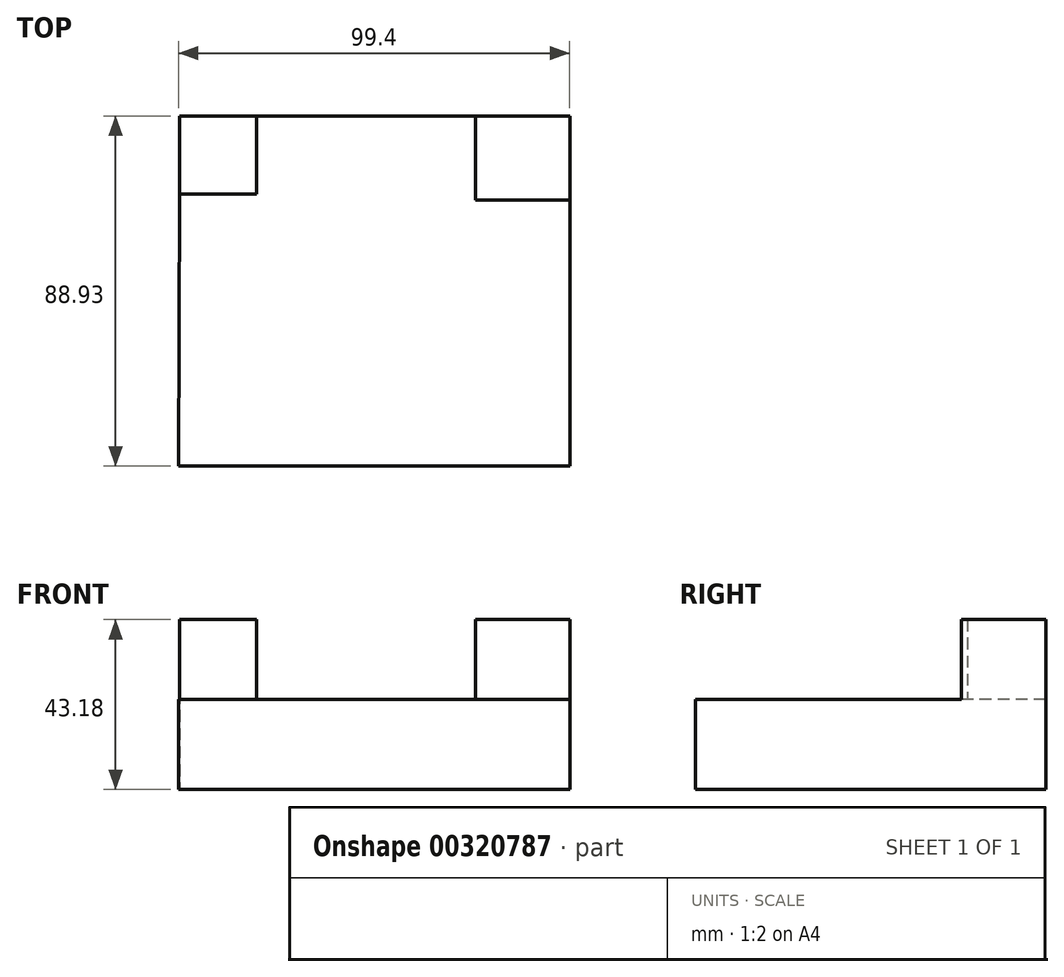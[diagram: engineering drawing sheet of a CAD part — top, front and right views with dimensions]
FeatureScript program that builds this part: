
annotation { "Feature Type Name" : "Feature", "Feature Type Description" : "" }
export const myFeature = defineFeature(function(context is Context, id is Id, definition is map)
    precondition{}
    {
        {
            var Q0;
            Q0=qCreatedBy(makeId("Top.planeOp"),FACE);
            var sketch = newSketch(context, id + "F0", { "sketchPlane" : qUnion([Q0])});
            skLineSegment(sketch, "E0", {"start": v(-45.8, -41.68) * mm, "end": v(53.6, -41.68) * mm});
            skLineSegment(sketch, "E1", {"start": v(53.6, -41.68) * mm, "end": v(53.6, 47.25) * mm});
            skLineSegment(sketch, "E2", {"start": v(53.6, 47.25) * mm, "end": v(-45.5, 47.25) * mm});
            skLineSegment(sketch, "E3", {"start": v(-45.8, -41.68) * mm, "end": v(-45.5, 47.25) * mm});
            skSolve(sketch);
        }
        {
            var Q0;
            Q0=makeQuery(id+"F0.imprint","IMPRINT",FACE,{"disambiguationData":[TD([[makeQuery(id+"F0.imprint","IMPRINT",EDGE,{"derivedFrom":sQuery(id+"F0.wireOp",EDGE,"E0")}),1.0]])]});
            extrude(context, id + "F1", {"entities" : qUnion([Q0]), "depth" : 22.86 * mm});
        }
        {
            var Q0;
            Q0=makeQuery(id+"F1.opExtrude","CAP_FACE",FACE,{"disambiguationData":[OSD([sQuery(id+"F0.wireOp",EDGE,"E0"),sQuery(id+"F0.wireOp",EDGE,"E1"),sQuery(id+"F0.wireOp",EDGE,"E2"),sQuery(id+"F0.wireOp",EDGE,"E3")])],"isStart":false});
            var sketch = newSketch(context, id + "F2", { "sketchPlane" : qUnion([Q0])});
            skLineSegment(sketch, "E4", {"start": v(29.71, 47.25) * mm, "end": v(29.71, 25.84) * mm});
            skLineSegment(sketch, "E5", {"start": v(29.71, 25.84) * mm, "end": v(53.6, 25.84) * mm});
            skSolve(sketch);
        }
        {
            var Q0;
            {var subQ0=sQuery(id+"F2.wireOp",EDGE,"E4");Q0=makeQuery(id+"F2.imprint","IMPRINT",FACE,{"disambiguationData":[TD([[makeQuery(id+"F2.imprint","IMPRINT",EDGE,{"derivedFrom":subQ0}),1.0]])]});}
            extrude(context, id + "F3", {"entities" : qUnion([Q0]), "operationType" : NewBodyOperationType.ADD, "depth" : 20.32 * mm});
        }
        {
            var Q0;
            Q0=makeQuery(id+"F1.opExtrude","CAP_FACE",FACE,{"disambiguationData":[OSD([sQuery(id+"F0.wireOp",EDGE,"E0"),sQuery(id+"F0.wireOp",EDGE,"E1"),sQuery(id+"F0.wireOp",EDGE,"E2"),sQuery(id+"F0.wireOp",EDGE,"E3")])],"isStart":false});
            var sketch = newSketch(context, id + "F4", { "sketchPlane" : qUnion([Q0])});
            skLineSegment(sketch, "E6", {"start": v(-26, 47.25) * mm, "end": v(-26, 27.4) * mm});
            skLineSegment(sketch, "E7", {"start": v(-26, 27.4) * mm, "end": v(-45.58, 27.4) * mm});
            skSolve(sketch);
        }
        {
            var Q0;
            {var subQ0=sQuery(id+"F4.wireOp",EDGE,"E6");Q0=makeQuery(id+"F4.imprint","IMPRINT",FACE,{"disambiguationData":[TD([[makeQuery(id+"F4.imprint","IMPRINT",EDGE,{"derivedFrom":subQ0}),-1.0]])]});}
            extrude(context, id + "F5", {"entities" : qUnion([Q0]), "operationType" : NewBodyOperationType.ADD, "depth" : 20.32 * mm});
        }
    });
